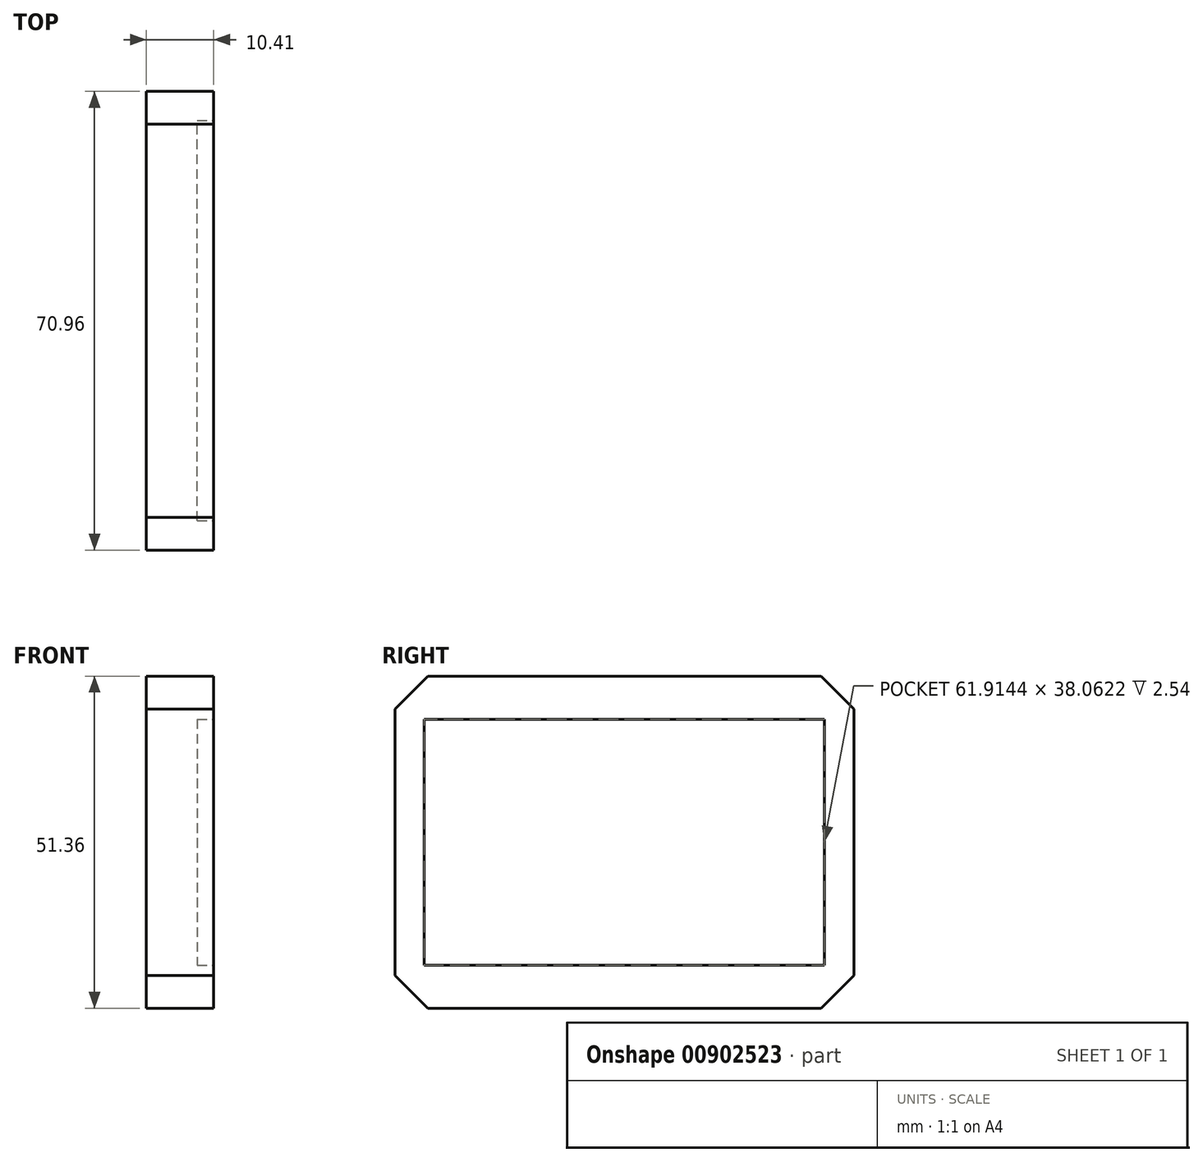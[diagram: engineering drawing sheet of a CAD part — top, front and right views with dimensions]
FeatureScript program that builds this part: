
annotation { "Feature Type Name" : "Feature", "Feature Type Description" : "" }
export const myFeature = defineFeature(function(context is Context, id is Id, definition is map)
    precondition{}
    {
        {
            var Q0;
            Q0=qCreatedBy(makeId("Right.planeOp"),FACE);
            var sketch = newSketch(context, id + "F0", { "sketchPlane" : qUnion([Q0])});
            skLineSegment(sketch, "E0.bottom", {"start": v(35.48, -25.68) * mm, "end": v(-35.48, -25.68) * mm});
            skLineSegment(sketch, "E0.top", {"start": v(35.48, 25.68) * mm, "end": v(-35.48, 25.68) * mm});
            skLineSegment(sketch, "E0.left", {"start": v(35.48, -25.68) * mm, "end": v(35.48, 25.68) * mm});
            skLineSegment(sketch, "E0.right", {"start": v(-35.48, -25.68) * mm, "end": v(-35.48, 25.68) * mm});
            skPoint(sketch, "E0.middle", {"position": v(0, 0) * mm});
            skSolve(sketch);
        }
        {
            var Q0;
            Q0 = qSketchRegion(id + "F0", true);
            var Q1;
            Q1=makeQuery(id+"F0.imprint","IMPRINT",FACE,{"disambiguationData":[TD([[makeQuery(id+"F0.imprint","IMPRINT",EDGE,{"derivedFrom":sQuery(id+"F0.wireOp",EDGE,"E0.bottom")}),-1.0]])]});
            extrude(context, id + "F1", {"entities" : qUnion([Q0, Q1]), "depth" : 76.2 * mm, "offsetDistance" : 25.4 * mm});
        }
        {
            var Q0;
            Q0=makeQuery(id+"F1.opExtrude","CAP_FACE",FACE,{"disambiguationData":[OSD([sQuery(id+"F0.wireOp",EDGE,"E0.bottom"),sQuery(id+"F0.wireOp",EDGE,"E0.top"),sQuery(id+"F0.wireOp",EDGE,"E0.left"),sQuery(id+"F0.wireOp",EDGE,"E0.right")])],"isStart":false});
            extrude(context, id + "F2", {"entities" : qUnion([Q0]), "operationType" : NewBodyOperationType.ADD, "depth" : 25.4 * mm, "offsetDistance" : 25.4 * mm});
        }
        {
            var Q0;
            Q0=makeQuery(id+"F2.opExtrude","CAP_FACE",FACE,{"disambiguationData":[OSD([sQuery(id+"F0.wireOp",EDGE,"E0.bottom"),sQuery(id+"F0.wireOp",EDGE,"E0.top"),sQuery(id+"F0.wireOp",EDGE,"E0.left"),sQuery(id+"F0.wireOp",EDGE,"E0.right")])],"isStart":false});
            extrude(context, id + "F3", {"entities" : qUnion([Q0]), "operationType" : NewBodyOperationType.REMOVE, "oppositeDirection" : true, "depth" : 40.4 * mm, "offsetDistance" : 25.4 * mm});
        }
        {
            var Q0;
            Q0=makeQuery(id+"F3.boolean.opBoolean","COPY",FACE,{"derivedFrom":makeQuery(id+"F3.opExtrude","CAP_FACE",FACE,{"disambiguationData":[OSD([sQuery(id+"F0.wireOp",EDGE,"E0.bottom"),sQuery(id+"F0.wireOp",EDGE,"E0.top"),sQuery(id+"F0.wireOp",EDGE,"E0.left"),sQuery(id+"F0.wireOp",EDGE,"E0.right")])],"isStart":false})});
            extrude(context, id + "F4", {"entities" : qUnion([Q0]), "operationType" : NewBodyOperationType.REMOVE, "oppositeDirection" : true, "depth" : 25.4 * mm, "offsetDistance" : 25.4 * mm});
        }
        {
            var Q0;
            Q0=makeQuery(id+"F4.boolean.opBoolean","COPY",FACE,{"derivedFrom":makeQuery(id+"F4.opExtrude","CAP_FACE",FACE,{"disambiguationData":[OSD([sQuery(id+"F0.wireOp",EDGE,"E0.bottom"),sQuery(id+"F0.wireOp",EDGE,"E0.top"),sQuery(id+"F0.wireOp",EDGE,"E0.left"),sQuery(id+"F0.wireOp",EDGE,"E0.right")])],"isStart":false})});
            var sketch = newSketch(context, id + "F5", { "sketchPlane" : qUnion([Q0])});
            skLineSegment(sketch, "E1.bottom", {"start": v(-30.96, 19.03) * mm, "end": v(30.96, 19.03) * mm});
            skLineSegment(sketch, "E1.top", {"start": v(-30.96, -19.03) * mm, "end": v(30.96, -19.03) * mm});
            skLineSegment(sketch, "E1.left", {"start": v(-30.96, 19.03) * mm, "end": v(-30.96, -19.03) * mm});
            skLineSegment(sketch, "E1.right", {"start": v(30.96, 19.03) * mm, "end": v(30.96, -19.03) * mm});
            skPoint(sketch, "E1.middle", {"position": v(0, 0) * mm});
            skSolve(sketch);
        }
        {
            var Q0;
            Q0 = qSketchRegion(id + "F5", true);
            extrude(context, id + "F6", {"entities" : qUnion([Q0]), "operationType" : NewBodyOperationType.REMOVE, "oppositeDirection" : true, "depth" : 2.54 * mm, "offsetDistance" : 25.4 * mm});
        }
        {
            var Q0;
            {var subQ0=sQuery(id+"F0.wireOp",EDGE,"E0.right");var subQ1=sQuery(id+"F0.wireOp",EDGE,"E0.top");Q0=makeQuery(id+"F2.boolean.opBoolean","MERGE",EDGE,{"derivedFrom":[makeQuery(id+"F1.opExtrude","SWEPT_EDGE",EDGE,{"disambiguationData":[OSD([subQ1,subQ0])]}),makeQuery(id+"F2.opExtrude","SWEPT_EDGE",EDGE,{"disambiguationData":[OSD([subQ1,subQ0])]})]});}
            chamfer(context, id + "F7", {"entities" : qUnion([Q0]), "width" : 5.08 * mm, "tangentPropagation" : true});
        }
        {
            var Q0;
            {var subQ0=sQuery(id+"F0.wireOp",EDGE,"E0.right");var subQ1=sQuery(id+"F0.wireOp",EDGE,"E0.bottom");Q0=makeQuery(id+"F2.boolean.opBoolean","MERGE",EDGE,{"derivedFrom":[makeQuery(id+"F1.opExtrude","SWEPT_EDGE",EDGE,{"disambiguationData":[OSD([subQ1,subQ0])]}),makeQuery(id+"F2.opExtrude","SWEPT_EDGE",EDGE,{"disambiguationData":[OSD([subQ1,subQ0])]})]});}
            chamfer(context, id + "F8", {"entities" : qUnion([Q0]), "width" : 5.08 * mm, "tangentPropagation" : true});
        }
        {
            var Q0;
            {var subQ0=sQuery(id+"F0.wireOp",EDGE,"E0.left");var subQ1=sQuery(id+"F0.wireOp",EDGE,"E0.top");Q0=makeQuery(id+"F2.boolean.opBoolean","MERGE",EDGE,{"derivedFrom":[makeQuery(id+"F1.opExtrude","SWEPT_EDGE",EDGE,{"disambiguationData":[OSD([subQ1,subQ0])]}),makeQuery(id+"F2.opExtrude","SWEPT_EDGE",EDGE,{"disambiguationData":[OSD([subQ1,subQ0])]})]});}
            chamfer(context, id + "F9", {"entities" : qUnion([Q0]), "width" : 5.08 * mm, "tangentPropagation" : true});
        }
        {
            var Q0;
            {var subQ0=sQuery(id+"F0.wireOp",EDGE,"E0.left");var subQ1=sQuery(id+"F0.wireOp",EDGE,"E0.bottom");Q0=makeQuery(id+"F2.boolean.opBoolean","MERGE",EDGE,{"derivedFrom":[makeQuery(id+"F1.opExtrude","SWEPT_EDGE",EDGE,{"disambiguationData":[OSD([subQ1,subQ0])]}),makeQuery(id+"F2.opExtrude","SWEPT_EDGE",EDGE,{"disambiguationData":[OSD([subQ1,subQ0])]})]});}
            chamfer(context, id + "F10", {"entities" : qUnion([Q0]), "width" : 5.08 * mm, "tangentPropagation" : true});
        }
        {
            var Q0;
            Q0=makeQuery(id+"F1.opExtrude","CAP_FACE",FACE,{"disambiguationData":[OSD([sQuery(id+"F0.wireOp",EDGE,"E0.bottom"),sQuery(id+"F0.wireOp",EDGE,"E0.top"),sQuery(id+"F0.wireOp",EDGE,"E0.left"),sQuery(id+"F0.wireOp",EDGE,"E0.right")])],"isStart":true});
            extrude(context, id + "F11", {"entities" : qUnion([Q0]), "operationType" : NewBodyOperationType.REMOVE, "oppositeDirection" : true, "depth" : 25.4 * mm, "offsetDistance" : 25.4 * mm});
        }
    });
